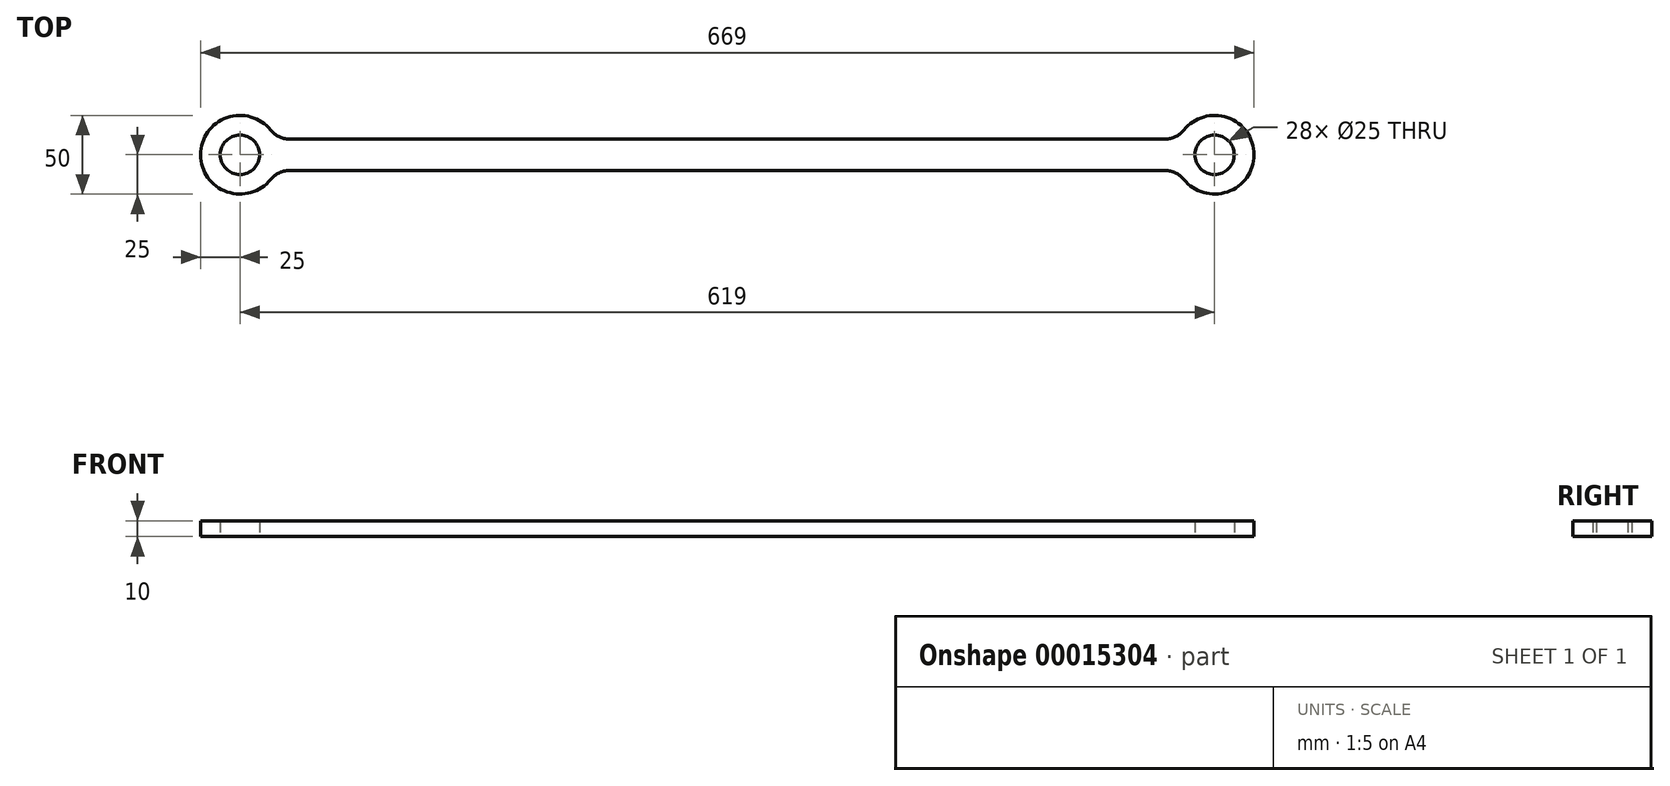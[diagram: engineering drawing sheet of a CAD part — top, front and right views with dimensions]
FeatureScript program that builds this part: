
annotation { "Feature Type Name" : "Feature", "Feature Type Description" : "" }
export const myFeature = defineFeature(function(context is Context, id is Id, definition is map)
    precondition{}
    {
        {
            var Q0;
            Q0=qCreatedBy(makeId("Top.planeOp"),FACE);
            var sketch = newSketch(context, id + "F0", { "sketchPlane" : qUnion([Q0])});
            skArc(sketch, "E0", {"start": v(19.52, 15.63) * mm, "mid": v(-25, 0) * mm, "end": v(19.52, -15.63) * mm});
            skArc(sketch, "E1", {"start": v(599.48, -15.63) * mm, "mid": v(644, 0) * mm, "end": v(599.48, 15.63) * mm});
            skLineSegment(sketch, "E2", {"start": v(31.22, 10) * mm, "end": v(587.78, 10) * mm});
            skLineSegment(sketch, "E3", {"start": v(0, 0) * mm, "end": v(619, 0) * mm, "construction": true});
            skLineSegment(sketch, "E4.MirrorCS", {"start": v(31.22, -10) * mm, "end": v(587.78, -10) * mm});
            skPoint(sketch, "E5.visualSharp", {"position": v(22.91, 10) * mm});
            skArc(sketch, "E5.filletArc", {"start": v(19.52, 15.62) * mm, "mid": v(24.73, 11.48) * mm, "end": v(31.22, 10) * mm});
            skPoint(sketch, "E6.visualSharp", {"position": v(22.91, -10) * mm});
            skArc(sketch, "E6.filletArc", {"start": v(31.22, -10) * mm, "mid": v(24.73, -11.48) * mm, "end": v(19.52, -15.62) * mm});
            skPoint(sketch, "E7.visualSharp", {"position": v(596.09, -10) * mm});
            skArc(sketch, "E7.filletArc", {"start": v(599.48, -15.63) * mm, "mid": v(594.27, -11.48) * mm, "end": v(587.78, -10) * mm});
            skPoint(sketch, "E8.visualSharp", {"position": v(596.09, 10) * mm});
            skArc(sketch, "E8.filletArc", {"start": v(587.78, 10) * mm, "mid": v(594.27, 11.48) * mm, "end": v(599.48, 15.63) * mm});
            skCircle(sketch, "E9", {"center": v(0, 0) * mm, "radius": 12.5 * mm});
            skCircle(sketch, "E10", {"center": v(619, 0) * mm, "radius": 12.5 * mm});
            skSolve(sketch);
        }
        {
            var Q0;
            Q0=qSketchRegion(id+"F0",true);
            extrude(context, id + "F1", {"entities" : qUnion([Q0]), "depth" : 10 * mm});
        }
    });
